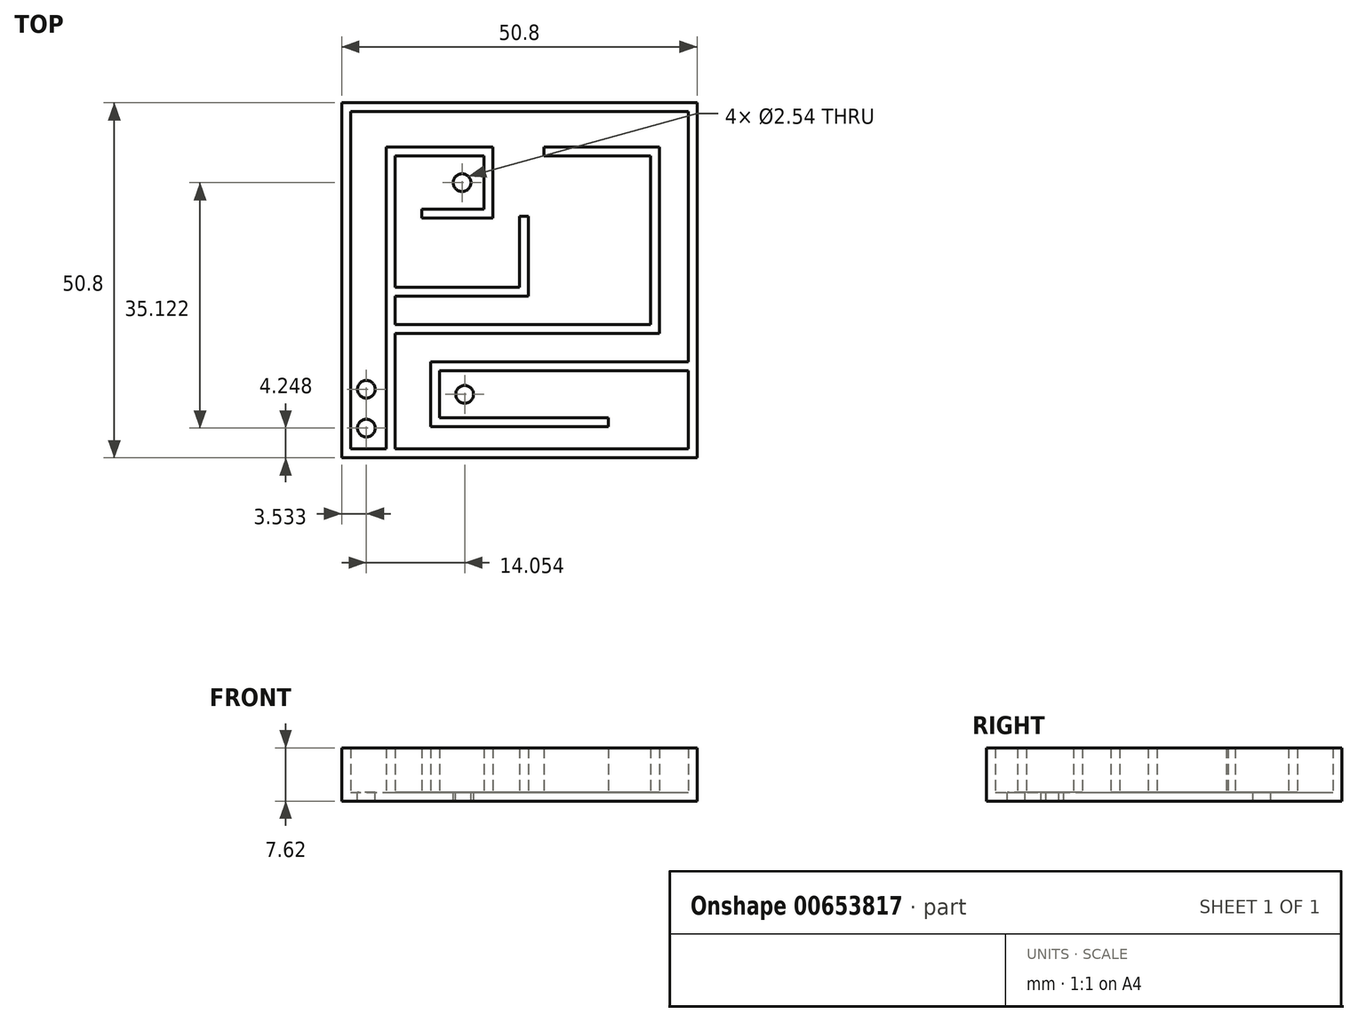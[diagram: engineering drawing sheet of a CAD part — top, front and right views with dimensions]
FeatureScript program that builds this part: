
annotation { "Feature Type Name" : "Feature", "Feature Type Description" : "" }
export const myFeature = defineFeature(function(context is Context, id is Id, definition is map)
    precondition{}
    {
        {
            var Q0;
            Q0=qCreatedBy(makeId("Top.planeOp"),FACE);
            var sketch = newSketch(context, id + "F0", { "sketchPlane" : qUnion([Q0])});
            skLineSegment(sketch, "E0.bottom", {"start": v(0, 0) * mm, "end": v(50.8, 0) * mm});
            skLineSegment(sketch, "E0.top", {"start": v(0, 50.8) * mm, "end": v(50.8, 50.8) * mm});
            skLineSegment(sketch, "E0.left", {"start": v(0, 0) * mm, "end": v(0, 50.8) * mm});
            skLineSegment(sketch, "E0.right", {"start": v(50.8, 0) * mm, "end": v(50.8, 50.8) * mm});
            skSolve(sketch);
        }
        {
            var Q0;
            Q0=makeQuery(id+"F0.imprint","IMPRINT",FACE,{"disambiguationData":[TD([[makeQuery(id+"F0.imprint","IMPRINT",EDGE,{"derivedFrom":sQuery(id+"F0.wireOp",EDGE,"E0.bottom")}),1.0]])]});
            extrude(context, id + "F1", {"entities" : qUnion([Q0]), "depth" : 7.62 * mm, "offsetDistance" : 25.4 * mm});
        }
        {
            var Q0;
            Q0=makeQuery(id+"F1.opExtrude","CAP_FACE",FACE,{"disambiguationData":[OSD([sQuery(id+"F0.wireOp",EDGE,"E0.bottom"),sQuery(id+"F0.wireOp",EDGE,"E0.top"),sQuery(id+"F0.wireOp",EDGE,"E0.left"),sQuery(id+"F0.wireOp",EDGE,"E0.right")])],"isStart":false});
            shell(context, id + "F2", {"entities" : qUnion([Q0]), "thickness" : 1.27 * mm});
        }
        {
            var Q0;
            Q0=makeQuery(id+"F2.opShell","OFFSET_FACE",FACE,{"disambiguationData":[OSD([sQuery(id+"F0.wireOp",EDGE,"E0.bottom"),sQuery(id+"F0.wireOp",EDGE,"E0.top"),sQuery(id+"F0.wireOp",EDGE,"E0.left"),sQuery(id+"F0.wireOp",EDGE,"E0.right")])]});
            var sketch = newSketch(context, id + "F3", { "sketchPlane" : qUnion([Q0])});
            skLineSegment(sketch, "E1.bottom", {"start": v(6.35, 1.27) * mm, "end": v(7.62, 1.27) * mm});
            skLineSegment(sketch, "E1.top", {"start": v(6.35, 44.45) * mm, "end": v(7.62, 44.45) * mm});
            skLineSegment(sketch, "E1.left", {"start": v(6.35, 1.27) * mm, "end": v(6.35, 44.45) * mm});
            skLineSegment(sketch, "E1.right", {"start": v(7.62, 1.27) * mm, "end": v(7.62, 44.45) * mm});
            skSolve(sketch);
        }
        {
            var Q0;
            Q0=makeQuery(id+"F3.imprint","IMPRINT",FACE,{"disambiguationData":[TD([[makeQuery(id+"F3.imprint","IMPRINT",EDGE,{"derivedFrom":sQuery(id+"F3.wireOp",EDGE,"E1.bottom")}),1.0]])]});
            extrude(context, id + "F4", {"entities" : qUnion([Q0]), "operationType" : NewBodyOperationType.ADD, "depth" : 6.35 * mm, "offsetDistance" : 25.4 * mm});
        }
        {
            var Q0;
            Q0=makeQuery(id+"F2.opShell","OFFSET_FACE",FACE,{"disambiguationData":[OSD([sQuery(id+"F0.wireOp",EDGE,"E0.bottom"),sQuery(id+"F0.wireOp",EDGE,"E0.top"),sQuery(id+"F0.wireOp",EDGE,"E0.left"),sQuery(id+"F0.wireOp",EDGE,"E0.right")])]});
            var sketch = newSketch(context, id + "F5", { "sketchPlane" : qUnion([Q0])});
            skCircle(sketch, "E2", {"center": v(3.53, 9.8) * mm, "radius": 1.27 * mm});
            skCircle(sketch, "E3", {"center": v(3.53, 4.25) * mm, "radius": 1.27 * mm});
            skSolve(sketch);
        }
        {
            var Q0;
            Q0 = qSketchRegion(id + "F5", true);
            var Q1;
            Q1=sQuery(id+"F5.wireOp",EDGE,"E2");
            var Q2;
            Q2=sQuery(id+"F5.wireOp",EDGE,"E3");
            extrude(context, id + "F6", {"entities" : qUnion([Q0]), "operationType" : NewBodyOperationType.REMOVE, "surfaceEntities" : qUnion([Q1, Q2]), "oppositeDirection" : true, "depth" : 25.4 * mm, "offsetDistance" : 25.4 * mm});
        }
        {
            var Q0;
            Q0=makeQuery(id+"F2.opShell","OFFSET_FACE",FACE,{"disambiguationData":[OSD([sQuery(id+"F0.wireOp",EDGE,"E0.bottom"),sQuery(id+"F0.wireOp",EDGE,"E0.top"),sQuery(id+"F0.wireOp",EDGE,"E0.left"),sQuery(id+"F0.wireOp",EDGE,"E0.right")])]});
            var sketch = newSketch(context, id + "F7", { "sketchPlane" : qUnion([Q0])});
            skLineSegment(sketch, "E4.bottom", {"start": v(7.62, 44.45) * mm, "end": v(20.32, 44.45) * mm});
            skLineSegment(sketch, "E4.top", {"start": v(7.62, 43.18) * mm, "end": v(20.32, 43.18) * mm});
            skLineSegment(sketch, "E4.left", {"start": v(7.62, 44.45) * mm, "end": v(7.62, 43.18) * mm});
            skLineSegment(sketch, "E4.right", {"start": v(20.32, 44.45) * mm, "end": v(20.32, 43.18) * mm});
            skLineSegment(sketch, "E5.bottom", {"start": v(20.32, 44.45) * mm, "end": v(21.59, 44.45) * mm});
            skLineSegment(sketch, "E5.top", {"start": v(20.32, 35.56) * mm, "end": v(21.59, 35.56) * mm});
            skLineSegment(sketch, "E5.left", {"start": v(20.32, 44.45) * mm, "end": v(20.32, 35.56) * mm});
            skLineSegment(sketch, "E5.right", {"start": v(21.59, 44.45) * mm, "end": v(21.59, 35.56) * mm});
            skLineSegment(sketch, "E6.bottom", {"start": v(21.59, 35.56) * mm, "end": v(11.43, 35.56) * mm});
            skLineSegment(sketch, "E6.top", {"start": v(21.59, 34.3) * mm, "end": v(11.43, 34.3) * mm});
            skLineSegment(sketch, "E6.left", {"start": v(21.59, 35.56) * mm, "end": v(21.59, 34.3) * mm});
            skLineSegment(sketch, "E6.right", {"start": v(11.43, 35.56) * mm, "end": v(11.43, 34.3) * mm});
            skSolve(sketch);
        }
        {
            var Q0;
            Q0 = qSketchRegion(id + "F7", true);
            extrude(context, id + "F8", {"entities" : qUnion([Q0]), "operationType" : NewBodyOperationType.ADD, "depth" : 6.35 * mm, "offsetDistance" : 25.4 * mm});
        }
        {
            var Q0;
            Q0=makeQuery(id+"F2.opShell","OFFSET_FACE",FACE,{"disambiguationData":[OSD([sQuery(id+"F0.wireOp",EDGE,"E0.bottom"),sQuery(id+"F0.wireOp",EDGE,"E0.top"),sQuery(id+"F0.wireOp",EDGE,"E0.left"),sQuery(id+"F0.wireOp",EDGE,"E0.right")])]});
            var sketch = newSketch(context, id + "F9", { "sketchPlane" : qUnion([Q0])});
            skCircle(sketch, "E7", {"center": v(17.23, 39.37) * mm, "radius": 1.27 * mm});
            skPoint(sketch, "E7.centerSnap0", {"position": v(21.59, 39.37) * mm});
            skSolve(sketch);
        }
        {
            var Q0;
            Q0 = qSketchRegion(id + "F9", true);
            extrude(context, id + "F10", {"entities" : qUnion([Q0]), "operationType" : NewBodyOperationType.REMOVE, "oppositeDirection" : true, "depth" : 25.4 * mm, "offsetDistance" : 25.4 * mm});
        }
        {
            var Q0;
            Q0=makeQuery(id+"F2.opShell","OFFSET_FACE",FACE,{"disambiguationData":[OSD([sQuery(id+"F0.wireOp",EDGE,"E0.bottom"),sQuery(id+"F0.wireOp",EDGE,"E0.top"),sQuery(id+"F0.wireOp",EDGE,"E0.left"),sQuery(id+"F0.wireOp",EDGE,"E0.right")])]});
            var sketch = newSketch(context, id + "F11", { "sketchPlane" : qUnion([Q0])});
            skLineSegment(sketch, "E8.bottom", {"start": v(28.9, 43.18) * mm, "end": v(44.15, 43.18) * mm});
            skLineSegment(sketch, "E8.top", {"start": v(28.9, 44.45) * mm, "end": v(44.15, 44.45) * mm});
            skLineSegment(sketch, "E8.left", {"start": v(28.9, 43.18) * mm, "end": v(28.9, 44.45) * mm});
            skLineSegment(sketch, "E8.right", {"start": v(44.15, 43.18) * mm, "end": v(44.15, 44.45) * mm});
            skLineSegment(sketch, "E9.bottom", {"start": v(44.15, 44.45) * mm, "end": v(45.42, 44.45) * mm});
            skLineSegment(sketch, "E9.top", {"start": v(44.15, 19.05) * mm, "end": v(45.42, 19.05) * mm});
            skLineSegment(sketch, "E9.left", {"start": v(44.15, 44.45) * mm, "end": v(44.15, 19.05) * mm});
            skLineSegment(sketch, "E9.right", {"start": v(45.42, 44.45) * mm, "end": v(45.42, 19.05) * mm});
            skLineSegment(sketch, "E10.bottom", {"start": v(45.42, 19.05) * mm, "end": v(7.62, 19.05) * mm});
            skLineSegment(sketch, "E10.top", {"start": v(45.42, 17.78) * mm, "end": v(7.62, 17.78) * mm});
            skLineSegment(sketch, "E10.left", {"start": v(45.42, 19.05) * mm, "end": v(45.42, 17.78) * mm});
            skLineSegment(sketch, "E10.right", {"start": v(7.62, 19.05) * mm, "end": v(7.62, 17.78) * mm});
            skLineSegment(sketch, "E11.bottom", {"start": v(7.62, 24.38) * mm, "end": v(25.4, 24.38) * mm});
            skLineSegment(sketch, "E11.top", {"start": v(7.62, 23.1) * mm, "end": v(25.4, 23.1) * mm});
            skLineSegment(sketch, "E11.left", {"start": v(7.62, 24.38) * mm, "end": v(7.62, 23.1) * mm});
            skLineSegment(sketch, "E11.right", {"start": v(25.4, 24.38) * mm, "end": v(25.4, 23.1) * mm});
            skLineSegment(sketch, "E12.bottom", {"start": v(25.4, 23.1) * mm, "end": v(26.67, 23.1) * mm});
            skLineSegment(sketch, "E12.top", {"start": v(25.4, 34.54) * mm, "end": v(26.67, 34.54) * mm});
            skLineSegment(sketch, "E12.left", {"start": v(25.4, 23.1) * mm, "end": v(25.4, 34.54) * mm});
            skLineSegment(sketch, "E12.right", {"start": v(26.67, 23.1) * mm, "end": v(26.67, 34.54) * mm});
            skSolve(sketch);
        }
        {
            var Q0;
            Q0 = qSketchRegion(id + "F11", true);
            extrude(context, id + "F12", {"entities" : qUnion([Q0]), "operationType" : NewBodyOperationType.ADD, "depth" : 6.35 * mm, "offsetDistance" : 25.4 * mm});
        }
        {
            var Q0;
            Q0=makeQuery(id+"F2.opShell","OFFSET_FACE",FACE,{"disambiguationData":[OSD([sQuery(id+"F0.wireOp",EDGE,"E0.bottom"),sQuery(id+"F0.wireOp",EDGE,"E0.top"),sQuery(id+"F0.wireOp",EDGE,"E0.left"),sQuery(id+"F0.wireOp",EDGE,"E0.right")])]});
            var sketch = newSketch(context, id + "F13", { "sketchPlane" : qUnion([Q0])});
            skLineSegment(sketch, "E13.bottom", {"start": v(13.97, 13.72) * mm, "end": v(12.7, 13.72) * mm});
            skLineSegment(sketch, "E13.top", {"start": v(13.97, 5.72) * mm, "end": v(12.7, 5.72) * mm});
            skLineSegment(sketch, "E13.left", {"start": v(13.97, 13.72) * mm, "end": v(13.97, 5.72) * mm});
            skLineSegment(sketch, "E13.right", {"start": v(12.7, 13.72) * mm, "end": v(12.7, 5.72) * mm});
            skLineSegment(sketch, "E14.bottom", {"start": v(12.7, 5.72) * mm, "end": v(38.1, 5.72) * mm});
            skLineSegment(sketch, "E14.top", {"start": v(12.7, 4.45) * mm, "end": v(38.1, 4.45) * mm});
            skLineSegment(sketch, "E14.left", {"start": v(12.7, 5.72) * mm, "end": v(12.7, 4.45) * mm});
            skLineSegment(sketch, "E14.right", {"start": v(38.1, 5.72) * mm, "end": v(38.1, 4.45) * mm});
            skLineSegment(sketch, "E15.bottom", {"start": v(13.97, 13.72) * mm, "end": v(49.53, 13.72) * mm});
            skLineSegment(sketch, "E15.top", {"start": v(13.97, 12.44) * mm, "end": v(49.53, 12.44) * mm});
            skLineSegment(sketch, "E15.left", {"start": v(13.97, 13.72) * mm, "end": v(13.97, 12.44) * mm});
            skLineSegment(sketch, "E15.right", {"start": v(49.53, 13.72) * mm, "end": v(49.53, 12.44) * mm});
            skLineSegment(sketch, "E16", {"start": v(13.97, 5.72) * mm, "end": v(13.97, 12.44) * mm});
            skCircle(sketch, "E17", {"center": v(17.59, 9.08) * mm, "radius": 1.27 * mm});
            skPoint(sketch, "E17.centerSnap0", {"position": v(13.97, 9.08) * mm});
            skSolve(sketch);
        }
        {
            var Q0;
            Q0 = qSketchRegion(id + "F13", true);
            extrude(context, id + "F14", {"entities" : qUnion([Q0]), "operationType" : NewBodyOperationType.ADD, "depth" : 6.35 * mm, "offsetDistance" : 25.4 * mm});
        }
        {
            var Q0;
            Q0=makeQuery(id+"F14.opExtrude","CAP_FACE",FACE,{"disambiguationData":[OSD([sQuery(id+"F13.wireOp",EDGE,"E17")])],"isStart":false});
            extrude(context, id + "F15", {"entities" : qUnion([Q0]), "operationType" : NewBodyOperationType.REMOVE, "oppositeDirection" : true, "depth" : 25.4 * mm, "offsetDistance" : 25.4 * mm});
        }
    });
